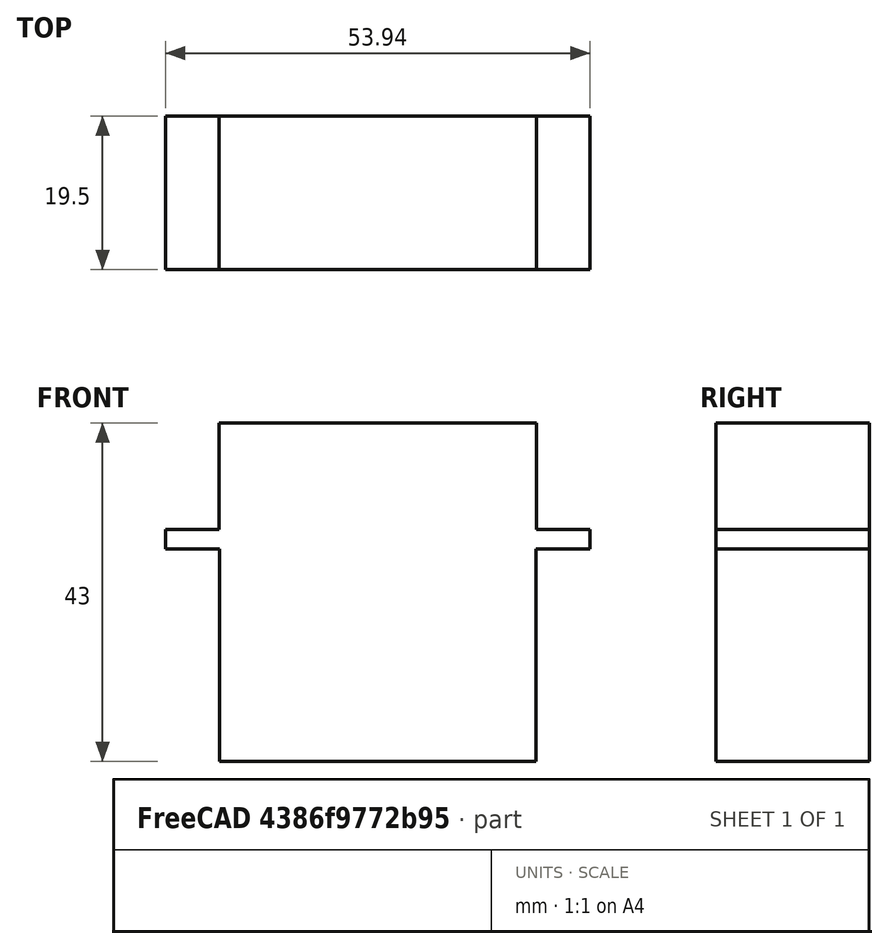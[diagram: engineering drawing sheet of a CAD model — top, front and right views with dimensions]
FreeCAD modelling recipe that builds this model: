
FCSTD DOCUMENT  (FreeCAD 0.20R29410 (Git))
Label: servo
License: All rights reserved
LicenseURL: http://en.wikipedia.org/wiki/All_rights_reserved
objects: Sketcher::SketchObject×1, PartDesign::Pad×1, PartDesign::Body×1
note: 4 computed .brp shape members not serialized (recipe doc carries the construction recipe); baked Part::Feature solids carry a one-line shape summary decoded from their .brp

FEATURE [Sketcher::SketchObject] Sketch
  FullyConstrained = false
  MapMode = 5
  Placement = pos=(0,0,0) rot=(1,0,0;1.5708rad)
  Support = -> [XZ_Plane]
  sketch-geometry (15):
    g0: LineSegment StartX=-20.1217 StartY=13.5 StartZ=0 EndX=-20.1217 EndY=-13.5 EndZ=0
    g1: LineSegment StartX=-20.1217 StartY=-13.5 StartZ=0 EndX=20.1217 EndY=-13.5 EndZ=0
    g2: LineSegment StartX=20.1217 StartY=-13.5 StartZ=0 EndX=20.1217 EndY=13.5 EndZ=0
    g3: GeomPoint X=0 Y=0 Z=0
    g4: LineSegment StartX=-26.9717 StartY=16 StartZ=0 EndX=-26.9717 EndY=13.5 EndZ=0
    g5: LineSegment StartX=26.9717 StartY=13.5 StartZ=0 EndX=26.9717 EndY=16 EndZ=0
    g6: GeomPoint X=0 Y=14.75 Z=0
    g7: LineSegment StartX=-20.15 StartY=29.5 StartZ=0 EndX=-20.15 EndY=16 EndZ=0
    g8: LineSegment StartX=20.15 StartY=16 StartZ=0 EndX=20.15 EndY=29.5 EndZ=0
    g9: LineSegment StartX=20.15 StartY=29.5 StartZ=0 EndX=-20.15 EndY=29.5 EndZ=0
    g10: GeomPoint X=0 Y=22.75 Z=0
    g11: LineSegment StartX=-26.9717 StartY=13.5 StartZ=0 EndX=-20.1217 EndY=13.5 EndZ=0
    g12: LineSegment StartX=26.9717 StartY=13.5 StartZ=0 EndX=20.1217 EndY=13.5 EndZ=0
    g13: LineSegment StartX=-20.15 StartY=16 StartZ=0 EndX=-26.9717 EndY=16 EndZ=0
    g14: LineSegment StartX=20.15 StartY=16 StartZ=0 EndX=26.9717 EndY=16 EndZ=0
  constraints (37):
    c: Coincident(g0,g1)
    c: Coincident(g1,g2)
    c: Horizontal(g1)
    c: Vertical(g0)
    c: Vertical(g2)
    c: Symmetric(g1,g0,g3)
    c: Coincident(g3,g-1)
    c: Vertical(g4)
    c: Vertical(g5)
    c: Symmetric(g5,g4,g6)
    c: PointOnObject(g6,g-2)
    c: Distance(g2) = 27
    c: Distance(g5) = 2.5
    c: Coincident(g8,g9)
    c: Coincident(g9,g7)
    c: Horizontal(g9)
    c: Vertical(g7)
    c: Vertical(g8)
    c: Symmetric(g8,g7,g10)
    c: PointOnObject(g10,g-2)
    c: Distance(g9) = 40.3
    c: Distance(g8) = 13.5
    c: Coincident(g4,g11)
    c: Coincident(g11,g0)
    c: Coincident(g5,g12)
    c: Coincident(g12,g2)
    c: Coincident(g7,g13)
    c: Coincident(g13,g4)
    c: Coincident(g8,g14)
    c: Coincident(g14,g5)
    c: Perpendicular(g0,g11)
    c: Perpendicular(g7,g13)
    c: Perpendicular(g8,g14)
    c: Perpendicular(g2,g12)
    c: Distance(g4) = 2.5
    c: Distance(g0) = 27
    c: Distance(g11) = 6.85
FEATURE [PartDesign::Pad] Pad
  Direction = (0,-1,2e-16)
  Length = 19.5
  Length2 = 10
  Placement = pos=(0,0,0) rot=(1,0,0;1.5708rad)
  Profile = -> Sketch
  ReferenceAxis = -> Sketch [N_Axis]
  Type = 0
FEATURE [PartDesign::Body] Body
  Group = -> [Sketch,Pad]
  Origin = -> Origin
  Tip = -> Pad
